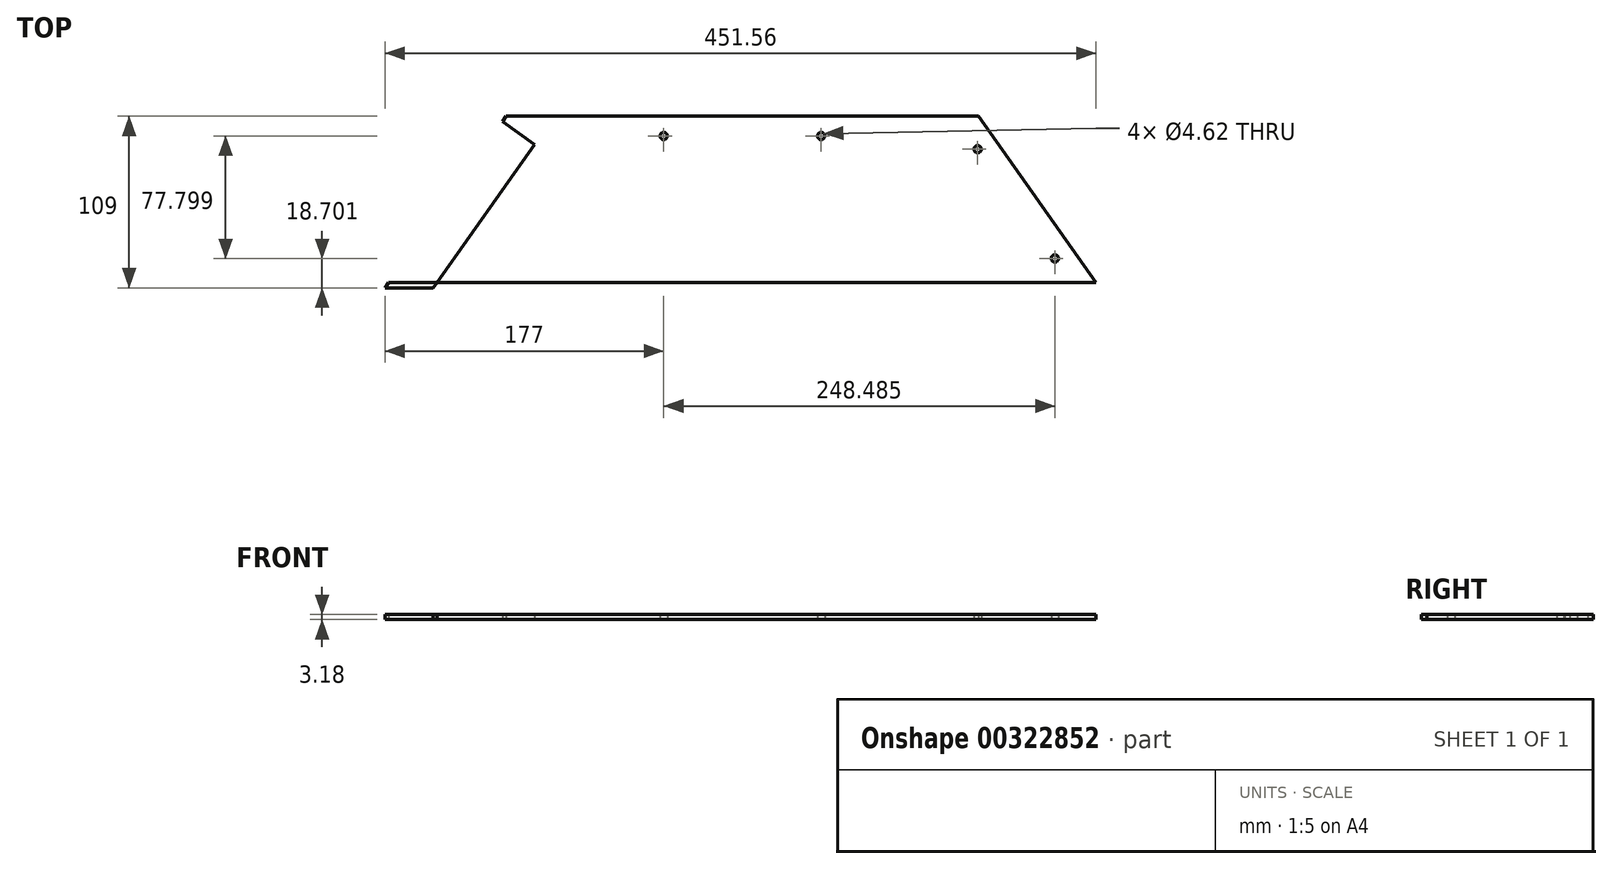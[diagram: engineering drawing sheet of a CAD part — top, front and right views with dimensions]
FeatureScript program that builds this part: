
annotation { "Feature Type Name" : "Feature", "Feature Type Description" : "" }
export const myFeature = defineFeature(function(context is Context, id is Id, definition is map)
    precondition{}
    {
        {
            var Q0;
            Q0=qCreatedBy(makeId("Top.planeOp"),FACE);
            var sketch = newSketch(context, id + "F0", { "sketchPlane" : qUnion([Q0])});
            skLineSegment(sketch, "E0.bottom", {"start": v(-423.4, 0) * mm, "end": v(-454, 0) * mm});
            skLineSegment(sketch, "E0.top", {"start": v(0, 109) * mm, "end": v(-454, 109) * mm});
            skLineSegment(sketch, "E0.left", {"start": v(0, 0) * mm, "end": v(0, 109) * mm});
            skLineSegment(sketch, "E0.right", {"start": v(-454, 0) * mm, "end": v(-454, 109) * mm});
            skLineSegment(sketch, "E1", {"start": v(-227, 109) * mm, "end": v(-77, 109) * mm});
            skLineSegment(sketch, "E2", {"start": v(-77, 109) * mm, "end": v(0, 0) * mm});
            skLineSegment(sketch, "E3", {"start": v(-227, 109) * mm, "end": v(-377, 109) * mm});
            skLineSegment(sketch, "E4", {"start": v(-377, 109) * mm, "end": v(-454, 0) * mm});
            skLineSegment(sketch, "E5.bottom", {"start": v(-177, 96.5) * mm, "end": v(-179.31, 96.5) * mm});
            skLineSegment(sketch, "E5.top", {"start": v(-177, 121.5) * mm, "end": v(-277, 121.5) * mm});
            skLineSegment(sketch, "E5.left", {"start": v(-177, 96.5) * mm, "end": v(-177, 98.81) * mm});
            skLineSegment(sketch, "E5.right", {"start": v(-277, 96.5) * mm, "end": v(-277, 98.81) * mm});
            skPoint(sketch, "E5.middle", {"position": v(-227, 109) * mm});
            skCircle(sketch, "E6", {"center": v(-277, 96.5) * mm, "radius": 2.31 * mm});
            skCircle(sketch, "E7", {"center": v(-177, 96.5) * mm, "radius": 2.31 * mm});
            skLineSegment(sketch, "E8.trimOffspring", {"start": v(-274.69, 96.5) * mm, "end": v(-277, 96.5) * mm});
            skLineSegment(sketch, "E9.trimOffspring", {"start": v(-277, 109) * mm, "end": v(-277, 121.5) * mm});
            skLineSegment(sketch, "E10.trimOffspring", {"start": v(-177, 109) * mm, "end": v(-177, 121.5) * mm});
            skLineSegment(sketch, "E11", {"start": v(-415.5, 54.5) * mm, "end": v(-386.65, 95.34) * mm});
            skLineSegment(sketch, "E12", {"start": v(-386.65, 95.34) * mm, "end": v(-435.7, 25.91) * mm});
            skLineSegment(sketch, "E13", {"start": v(-435.7, 25.91) * mm, "end": v(-425.48, 18.7) * mm});
            skLineSegment(sketch, "E14", {"start": v(-425.48, 18.7) * mm, "end": v(-376.44, 88.13) * mm});
            skLineSegment(sketch, "E15", {"start": v(-376.44, 88.13) * mm, "end": v(-386.65, 95.34) * mm});
            skCircle(sketch, "E16", {"center": v(-425.48, 18.7) * mm, "radius": 2.31 * mm});
            skCircle(sketch, "E17", {"center": v(-376.44, 88.13) * mm, "radius": 2.31 * mm});
            skLineSegment(sketch, "E18", {"start": v(-386.65, 95.34) * mm, "end": v(-379.44, 105.55) * mm});
            skLineSegment(sketch, "E19", {"start": v(-379.44, 105.55) * mm, "end": v(-359.02, 91.12) * mm});
            skLineSegment(sketch, "E20", {"start": v(-359.02, 91.12) * mm, "end": v(-423.4, 0) * mm});
            skLineSegment(sketch, "E21", {"start": v(-227, 109) * mm, "end": v(-227, 77.21) * mm});
            skCircle(sketch, "E22.MirrorC", {"center": v(-77.56, 88.13) * mm, "radius": 2.31 * mm});
            skCircle(sketch, "E23.MirrorC", {"center": v(-28.52, 18.7) * mm, "radius": 2.31 * mm});
            skLineSegment(sketch, "E24", {"start": v(-451.56, 3.45) * mm, "end": v(-2.44, 3.45) * mm});
            skSolve(sketch);
        }
        {
            var Q0;
            {var subQ11=sQuery(id+"F0.wireOp",EDGE,"E18");Q0=makeQuery(id+"F0.imprint","IMPRINT",FACE,{"disambiguationData":[TD([[makeQuery(id+"F0.imprint","IMPRINT",EDGE,{"derivedFrom":subQ11}),-1.0]])]});}
            var Q1;
            Q1=makeQuery(id+"F0.imprint","IMPRINT",FACE,{"disambiguationData":[TD([[makeQuery(id+"F0.imprint","IMPRINT",EDGE,{"derivedFrom":sQuery(id+"F0.wireOp",EDGE,"E0.bottom")}),-1.0]])]});
            var Q2;
            {var subQ1=sQuery(id+"F0.wireOp",EDGE,"E12");var subQ5=makeQuery(id+"F0.imprint","IMPRINT",VERTEX,{"derivedFrom":subQ1});Q2=makeQuery(id+"F0.imprint","IMPRINT",FACE,{"disambiguationData":[TD([[makeQuery(id+"F0.imprint","IMPRINT",EDGE,{"disambiguationData":[TD([[subQ5,1.0]])],"derivedFrom":subQ1}),1.0]])]});}
            var Q3;
            {var subQ7=sQuery(id+"F0.wireOp",EDGE,"E19");Q3=makeQuery(id+"F0.imprint","IMPRINT",FACE,{"disambiguationData":[TD([[makeQuery(id+"F0.imprint","IMPRINT",EDGE,{"derivedFrom":subQ7}),1.0]])]});}
            extrude(context, id + "F1", {"entities" : qUnion([Q0, Q1, Q2, Q3]), "depth" : 3.17 * mm});
        }
    });
